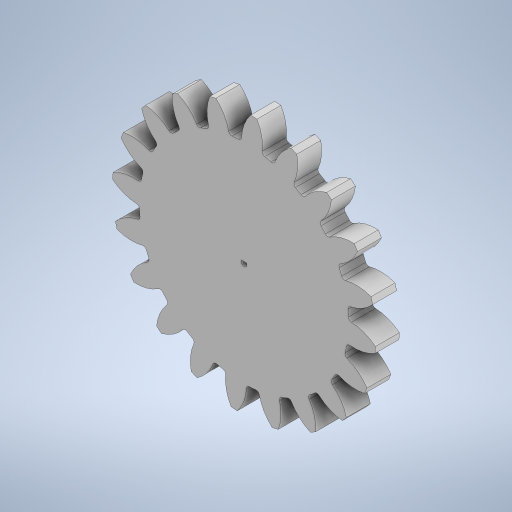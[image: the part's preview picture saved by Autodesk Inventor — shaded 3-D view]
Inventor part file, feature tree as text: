
AUTODESK INVENTOR PART (.ipt)
format: ipt  version: 2023.2 (Build 272271030, 271C)  size: 444,928 bytes
history: native  units: mm
features: extrude x1, fillet x1, pattern_circular x1, sketch x1
ambient origin geometry x8: Origin, YZ Plane, XZ Plane, XY Plane, X Axis, Y Axis, Z Axis, Center Point
bodies: Solid1 (feature_tree)
feature tree (4):
  extrude  "Extrusion1"  Depth=20.0mm TaperAngle=0.0deg
  fillet  "Fillet1"  Radius=2.61mm
  pattern_circular  "Circular Pattern1"  Count=20 Angle=360.0deg
  sketch  "Sketch1"  dims[d8=200.0mm d10=360.0deg d12=20.0mm d13=0.0mm d15=2.61mm d16=200.0mm d17=360.0deg d19=5.0mm d20=1.0mm]
